# Revit family: LSVB24
name_source: partatom
category: Lighting Fixtures
units: mm (PartAtom-declared; Revit-internal decimal feet)

## family parameters
Always vertical = Yes
Cut with Voids When Loaded = No
Host = Ceiling
Light Source = Yes
OmniClass Number = 23.80.70.11
OmniClass Title = Luminaries for Internal Lighting
Part Type = Normal
Room Calculation Point = No
Round Connector Dimension = Use Diameter
Shared = No

## types (1)
- LSVB24-LED840K035LUNV
    Apparent Load = 27 VA
    Assembly Code = D5020200
    Color Filter = 16777215
    Description = LED Sealed Vapour B
    Dimming Lamp Color Temperature Shift = <None>
    Emit from Line Length = 2' - 1 9/16"
    Housing Finish = Metal - Viscor - White
    Lamp = LED
    Lamp Wattage = 27 VA
    Length = 2' - 1 9/16"
    Lens Finsih = Polycarbonate - Viscor - Frosted Round
    Manufacturer = VISIONEERING by VISCOR
    Model = LSVB24
    Photometric Web File = LSVB24-LED840K035LUNV.ies
    Tilt Angle = 90.00°
    URL = https://www.viscor.com
    Voltage = 120 V
    Width = 0' - 3 7/8"

## geometry (parser evidence)
native form markers: Sweep x2
no freeform markers — native parametric forms only
